# Revit family: 303_R402X_+R460
name_source: partatom
category: Pipe Accessories
revit_build: Autodesk Revit 2018 (Build: 20170223_1515(x64)
units: mm (PartAtom-declared; Revit-internal decimal feet)

## family parameters
Always vertical = Yes
Cut with Voids When Loaded = No
Part Type = Valve - Breaks Into
Round Connector Dimension = Use Diameter
Shared = No
Work Plane-Based = No

## types (4) — shared parameters
CAT0 = Yes
Description = Straight valve with thermostatic option
L2D_Min = 3048 mm
M1 = 12 mm  [stored 0.0393701 ft]
Manufacturer = Giacomini
QmdConnectorList = 301;D;302;D1
TR2 = 15 mm  [stored 0.0492126 ft]
URL = http://www.giacomini.com
magiPartTypeId = 303
magiProductFamilyId = R402X*+R460
zero-valued in all types: MC_Default_elevation

## per-type parameters (varying)
- R402X132+R460: B3=9 mm  [stored 0.0295276 ft]; CenSd_K2_6=10 mm  [stored 0.0328084 ft]; CenSd_W2_6=12 mm  [stored 0.0393701 ft]; D=10 mm; D1=10 mm; G3=7 mm  [stored 0.0229659 ft]; J5=14 mm  [stored 0.0459318 ft]; K2=11 mm  [stored 0.0360892 ft]; K3=9 mm  [stored 0.0295276 ft]; L2=9 mm  [stored 0.0295276 ft]; L2D=57 mm; L4=7 mm  [stored 0.0229659 ft]; L5=9 mm  [stored 0.0295276 ft]; L6=4 mm  [stored 0.0131234 ft]; L61=2 mm  [stored 0.00656168 ft]; L61__ve=-2 mm  [stored -0.00656168 ft]; L6__ve=-4 mm; LC=54 mm  [stored 0.177165 ft]; LC1=29 mm; LC2=48 mm; LX=28 mm; R1=5 mm  [stored 0.0164042 ft]; TH2=84 mm; W2=14 mm  [stored 0.0459318 ft]; W2D=10 mm  [stored 0.0328084 ft]; W4=8 mm  [stored 0.0262467 ft]; X11=13 mm  [stored 0.0426509 ft]; Z1=10 mm  [stored 0.0328084 ft]
- R402X035+R460: B3=16 mm; CenSd_K2_6=17 mm; CenSd_W2_6=20 mm  [stored 0.0656168 ft]; D=25 mm; D1=25 mm; G3=14 mm  [stored 0.0459318 ft]; J5=23 mm; K2=20 mm  [stored 0.0656168 ft]; K3=16 mm; L2=12 mm  [stored 0.0393701 ft]; L2D=79 mm; L4=9 mm  [stored 0.0295276 ft]; L5=12 mm  [stored 0.0393701 ft]; L6=6 mm  [stored 0.019685 ft]; L61=3 mm  [stored 0.00984252 ft]; L61__ve=-3 mm; L6__ve=-6 mm; LC=64 mm; LC1=40 mm; LC2=66 mm; LX=42 mm; R1=13 mm  [stored 0.0426509 ft]; TH2=83 mm; W2=23 mm; W2D=25 mm  [stored 0.082021 ft]; W4=14 mm  [stored 0.0459318 ft]; X11=18 mm; Z1=17 mm
- R402X034+R460: B3=13 mm  [stored 0.0426509 ft]; CenSd_K2_6=14 mm  [stored 0.0459318 ft]; CenSd_W2_6=16 mm; D=20 mm; D1=20 mm; G3=12 mm  [stored 0.0393701 ft]; J5=19 mm; K2=16 mm; K3=13 mm  [stored 0.0426509 ft]; L2=10 mm  [stored 0.0328084 ft]; L2D=67 mm; L4=8 mm  [stored 0.0262467 ft]; L5=10 mm  [stored 0.0328084 ft]; L6=5 mm  [stored 0.0164042 ft]; L61=3 mm  [stored 0.00984252 ft]; L61__ve=-3 mm; L6__ve=-5 mm  [stored -0.0164042 ft]; LC=55 mm; LC1=34 mm; LC2=56 mm; LX=34 mm; R1=10 mm  [stored 0.0328084 ft]; TH2=79 mm; W2=19 mm; W2D=20 mm  [stored 0.0656168 ft]; W4=11 mm  [stored 0.0360892 ft]; X11=15 mm  [stored 0.0492126 ft]; Z1=14 mm  [stored 0.0459318 ft]
- R402X133+R460: B3=10 mm  [stored 0.0328084 ft]; CenSd_K2_6=11 mm  [stored 0.0360892 ft]; CenSd_W2_6=13 mm  [stored 0.0426509 ft]; D=15 mm; D1=15 mm; G3=9 mm  [stored 0.0295276 ft]; J5=15 mm  [stored 0.0492126 ft]; K2=13 mm  [stored 0.0426509 ft]; K3=10 mm  [stored 0.0328084 ft]; L2=10 mm  [stored 0.0328084 ft]; L2D=62 mm; L4=7 mm  [stored 0.0229659 ft]; L5=9 mm  [stored 0.0295276 ft]; L6=5 mm  [stored 0.0164042 ft]; L61=2 mm  [stored 0.00656168 ft]; L61__ve=-2 mm  [stored -0.00656168 ft]; L6__ve=-5 mm  [stored -0.0164042 ft]; LC=55 mm; LC1=31 mm; LC2=52 mm; LX=31 mm; R1=8 mm  [stored 0.0262467 ft]; TH2=83 mm; W2=15 mm  [stored 0.0492126 ft]; W2D=15 mm  [stored 0.0492126 ft]; W4=9 mm  [stored 0.0295276 ft]; X11=14 mm  [stored 0.0459318 ft]; Z1=11 mm  [stored 0.0360892 ft]

note: column(s) folded — value = type name in every type: magiProductCode, magiProductId

note: [stored X ft] marks values corroborated as IEEE doubles in the binary element streams (Revit-internal decimal feet)

## geometry (parser evidence)
native form markers: Sweep x2
no freeform markers — native parametric forms only
